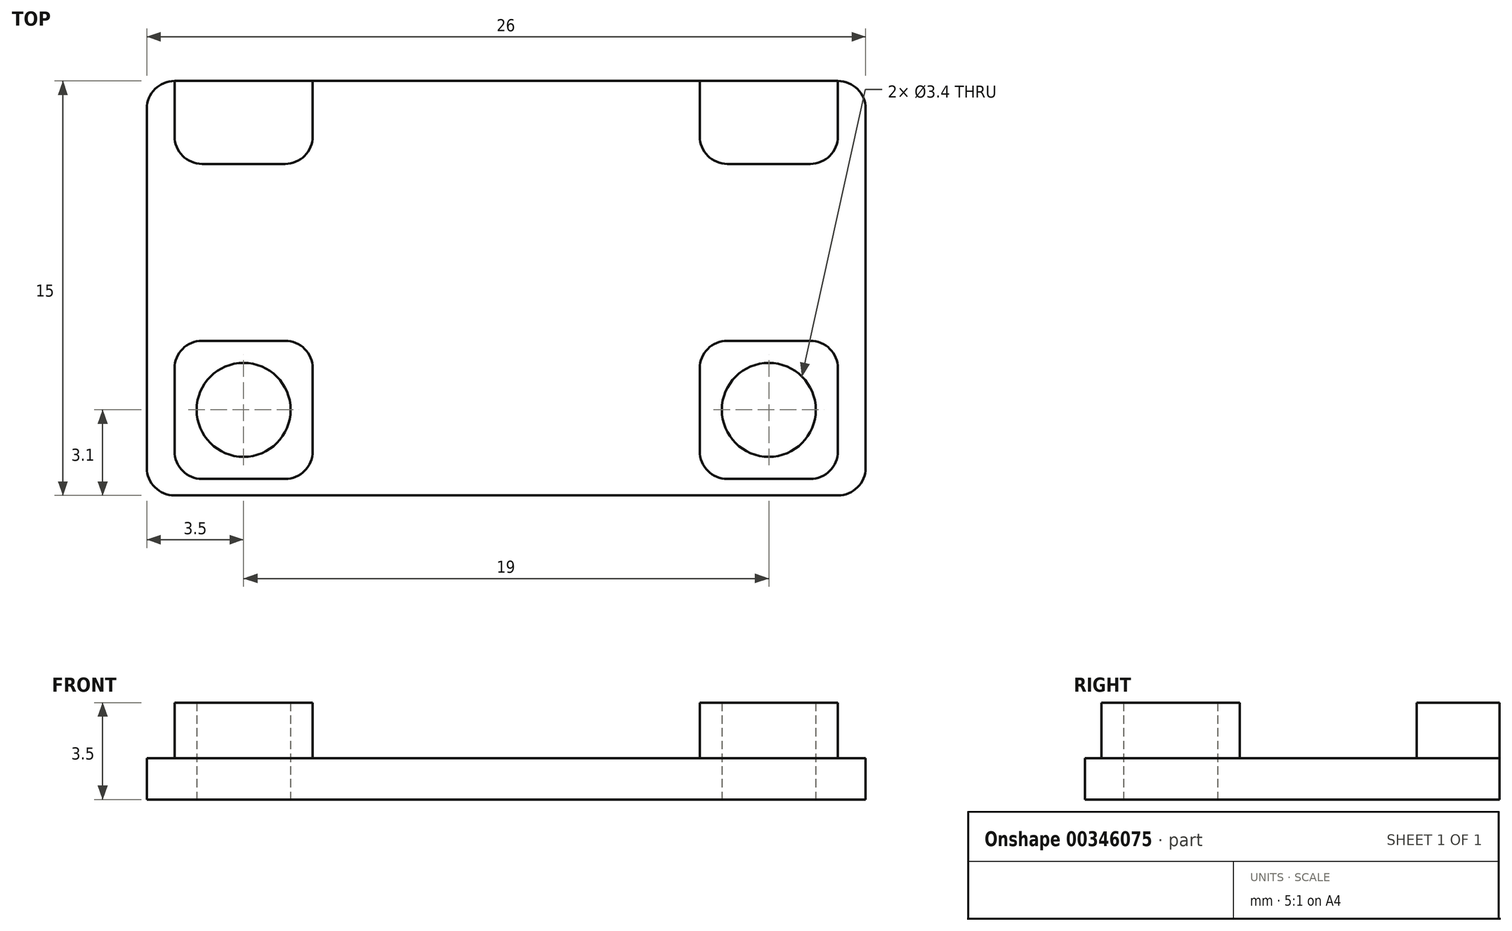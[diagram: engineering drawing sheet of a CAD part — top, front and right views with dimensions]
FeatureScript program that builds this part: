
annotation { "Feature Type Name" : "Feature", "Feature Type Description" : "" }
export const myFeature = defineFeature(function(context is Context, id is Id, definition is map)
    precondition{}
    {
        {
            var Q0;
            Q0=qCreatedBy(makeId("Top.planeOp"),FACE);
            var sketch = newSketch(context, id + "F0", { "sketchPlane" : qUnion([Q0])});
            skLineSegment(sketch, "E0", {"start": v(-26, 0) * mm, "end": v(0, 0) * mm});
            skLineSegment(sketch, "E1", {"start": v(0, 0) * mm, "end": v(0, -15) * mm});
            skLineSegment(sketch, "E2", {"start": v(-26, 0) * mm, "end": v(-26, -15) * mm});
            skLineSegment(sketch, "E3", {"start": v(-26, -15) * mm, "end": v(0, -15) * mm});
            skCircle(sketch, "E4", {"center": v(-22.5, -11.9) * mm, "radius": 1.7 * mm});
            skCircle(sketch, "E5", {"center": v(-3.5, -11.9) * mm, "radius": 1.7 * mm});
            skSolve(sketch);
        }
        {
            var Q0;
            Q0 = qSketchRegion(id + "F0", true);
            extrude(context, id + "F1", {"entities" : qUnion([Q0]), "depth" : 1.5 * mm});
        }
        {
            var Q0;
            Q0=makeQuery(id+"F1.opExtrude","CAP_FACE",FACE,{"disambiguationData":[OSD([sQuery(id+"F0.wireOp",EDGE,"E0"),sQuery(id+"F0.wireOp",EDGE,"E1"),sQuery(id+"F0.wireOp",EDGE,"E2"),sQuery(id+"F0.wireOp",EDGE,"E3"),sQuery(id+"F0.wireOp",EDGE,"E4"),sQuery(id+"F0.wireOp",EDGE,"E5")])],"isStart":false});
            var sketch = newSketch(context, id + "F2", { "sketchPlane" : qUnion([Q0])});
            skCircle(sketch, "E6", {"center": v(-22.5, -11.9) * mm, "radius": 1.7 * mm});
            skCircle(sketch, "E7", {"center": v(-3.5, -11.9) * mm, "radius": 1.7 * mm});
            skLineSegment(sketch, "E8.bottom", {"start": v(-25, -9.4) * mm, "end": v(-20, -9.4) * mm});
            skLineSegment(sketch, "E8.top", {"start": v(-25, -14.4) * mm, "end": v(-20, -14.4) * mm});
            skLineSegment(sketch, "E8.left", {"start": v(-25, -9.4) * mm, "end": v(-25, -14.4) * mm});
            skLineSegment(sketch, "E8.right", {"start": v(-20, -9.4) * mm, "end": v(-20, -14.4) * mm});
            skLineSegment(sketch, "E9.bottom", {"start": v(-6, -9.4) * mm, "end": v(-1, -9.4) * mm});
            skLineSegment(sketch, "E9.top", {"start": v(-6, -14.4) * mm, "end": v(-1, -14.4) * mm});
            skLineSegment(sketch, "E9.left", {"start": v(-6, -9.4) * mm, "end": v(-6, -14.4) * mm});
            skLineSegment(sketch, "E9.right", {"start": v(-1, -9.4) * mm, "end": v(-1, -14.4) * mm});
            skLineSegment(sketch, "E10.bottom", {"start": v(-25, 0) * mm, "end": v(-20, 0) * mm});
            skLineSegment(sketch, "E10.top", {"start": v(-25, -3) * mm, "end": v(-20, -3) * mm});
            skLineSegment(sketch, "E10.left", {"start": v(-25, 0) * mm, "end": v(-25, -3) * mm});
            skLineSegment(sketch, "E10.right", {"start": v(-20, 0) * mm, "end": v(-20, -3) * mm});
            skLineSegment(sketch, "E11.bottom", {"start": v(-6, 0) * mm, "end": v(-1, 0) * mm});
            skLineSegment(sketch, "E11.top", {"start": v(-6, -3) * mm, "end": v(-1, -3) * mm});
            skLineSegment(sketch, "E11.left", {"start": v(-6, 0) * mm, "end": v(-6, -3) * mm});
            skLineSegment(sketch, "E11.right", {"start": v(-1, 0) * mm, "end": v(-1, -3) * mm});
            skSolve(sketch);
        }
        {
            var Q0;
            Q0 = qSketchRegion(id + "F2", true);
            extrude(context, id + "F3", {"entities" : qUnion([Q0]), "operationType" : NewBodyOperationType.ADD, "depth" : 2 * mm});
        }
        {
            var Q0;
            Q0=makeQuery(id+"F1.opExtrude","SWEPT_EDGE",EDGE,{"disambiguationData":[OSD([sQuery(id+"F0.wireOp",EDGE,"E0"),sQuery(id+"F0.wireOp",EDGE,"E2")])]});
            var Q1;
            Q1=makeQuery(id+"F1.opExtrude","SWEPT_EDGE",EDGE,{"disambiguationData":[OSD([sQuery(id+"F0.wireOp",EDGE,"E2"),sQuery(id+"F0.wireOp",EDGE,"E3")])]});
            var Q2;
            Q2=makeQuery(id+"F1.opExtrude","SWEPT_EDGE",EDGE,{"disambiguationData":[OSD([sQuery(id+"F0.wireOp",EDGE,"E1"),sQuery(id+"F0.wireOp",EDGE,"E3")])]});
            var Q3;
            Q3=makeQuery(id+"F1.opExtrude","SWEPT_EDGE",EDGE,{"disambiguationData":[OSD([sQuery(id+"F0.wireOp",EDGE,"E0"),sQuery(id+"F0.wireOp",EDGE,"E1")])]});
            var Q4;
            Q4=makeQuery(id+"F3.opExtrude","SWEPT_EDGE",EDGE,{"disambiguationData":[OSD([sQuery(id+"F2.wireOp",EDGE,"E11.top"),sQuery(id+"F2.wireOp",EDGE,"E11.right")])]});
            var Q5;
            Q5=makeQuery(id+"F3.opExtrude","SWEPT_EDGE",EDGE,{"disambiguationData":[OSD([sQuery(id+"F2.wireOp",EDGE,"E11.top"),sQuery(id+"F2.wireOp",EDGE,"E11.left")])]});
            var Q6;
            Q6=makeQuery(id+"F3.opExtrude","SWEPT_EDGE",EDGE,{"disambiguationData":[OSD([sQuery(id+"F2.wireOp",EDGE,"E10.top"),sQuery(id+"F2.wireOp",EDGE,"E10.right")])]});
            var Q7;
            Q7=makeQuery(id+"F3.opExtrude","SWEPT_EDGE",EDGE,{"disambiguationData":[OSD([sQuery(id+"F2.wireOp",EDGE,"E10.top"),sQuery(id+"F2.wireOp",EDGE,"E10.left")])]});
            var Q8;
            Q8=makeQuery(id+"F3.opExtrude","SWEPT_EDGE",EDGE,{"disambiguationData":[OSD([sQuery(id+"F2.wireOp",EDGE,"E8.top"),sQuery(id+"F2.wireOp",EDGE,"E8.left")])]});
            var Q9;
            Q9=makeQuery(id+"F3.opExtrude","SWEPT_EDGE",EDGE,{"disambiguationData":[OSD([sQuery(id+"F2.wireOp",EDGE,"E8.bottom"),sQuery(id+"F2.wireOp",EDGE,"E8.left")])]});
            var Q10;
            Q10=makeQuery(id+"F3.opExtrude","SWEPT_EDGE",EDGE,{"disambiguationData":[OSD([sQuery(id+"F2.wireOp",EDGE,"E8.bottom"),sQuery(id+"F2.wireOp",EDGE,"E8.right")])]});
            var Q11;
            Q11=makeQuery(id+"F3.opExtrude","SWEPT_EDGE",EDGE,{"disambiguationData":[OSD([sQuery(id+"F2.wireOp",EDGE,"E8.top"),sQuery(id+"F2.wireOp",EDGE,"E8.right")])]});
            var Q12;
            Q12=makeQuery(id+"F3.opExtrude","SWEPT_EDGE",EDGE,{"disambiguationData":[OSD([sQuery(id+"F2.wireOp",EDGE,"E9.top"),sQuery(id+"F2.wireOp",EDGE,"E9.left")])]});
            var Q13;
            Q13=makeQuery(id+"F3.opExtrude","SWEPT_EDGE",EDGE,{"disambiguationData":[OSD([sQuery(id+"F2.wireOp",EDGE,"E9.top"),sQuery(id+"F2.wireOp",EDGE,"E9.right")])]});
            var Q14;
            Q14=makeQuery(id+"F3.opExtrude","SWEPT_EDGE",EDGE,{"disambiguationData":[OSD([sQuery(id+"F2.wireOp",EDGE,"E9.bottom"),sQuery(id+"F2.wireOp",EDGE,"E9.right")])]});
            var Q15;
            Q15=makeQuery(id+"F3.opExtrude","SWEPT_EDGE",EDGE,{"disambiguationData":[OSD([sQuery(id+"F2.wireOp",EDGE,"E9.bottom"),sQuery(id+"F2.wireOp",EDGE,"E9.left")])]});
            fillet(context, id + "F4", {"entities" : qUnion([Q0, Q1, Q2, Q3, Q4, Q5, Q6, Q7, Q8, Q9, Q10, Q11, Q12, Q13, Q14, Q15]), "radius" : 1 * mm, "tangentPropagation" : true, "allowEdgeOverflow" : false});
        }
    });
